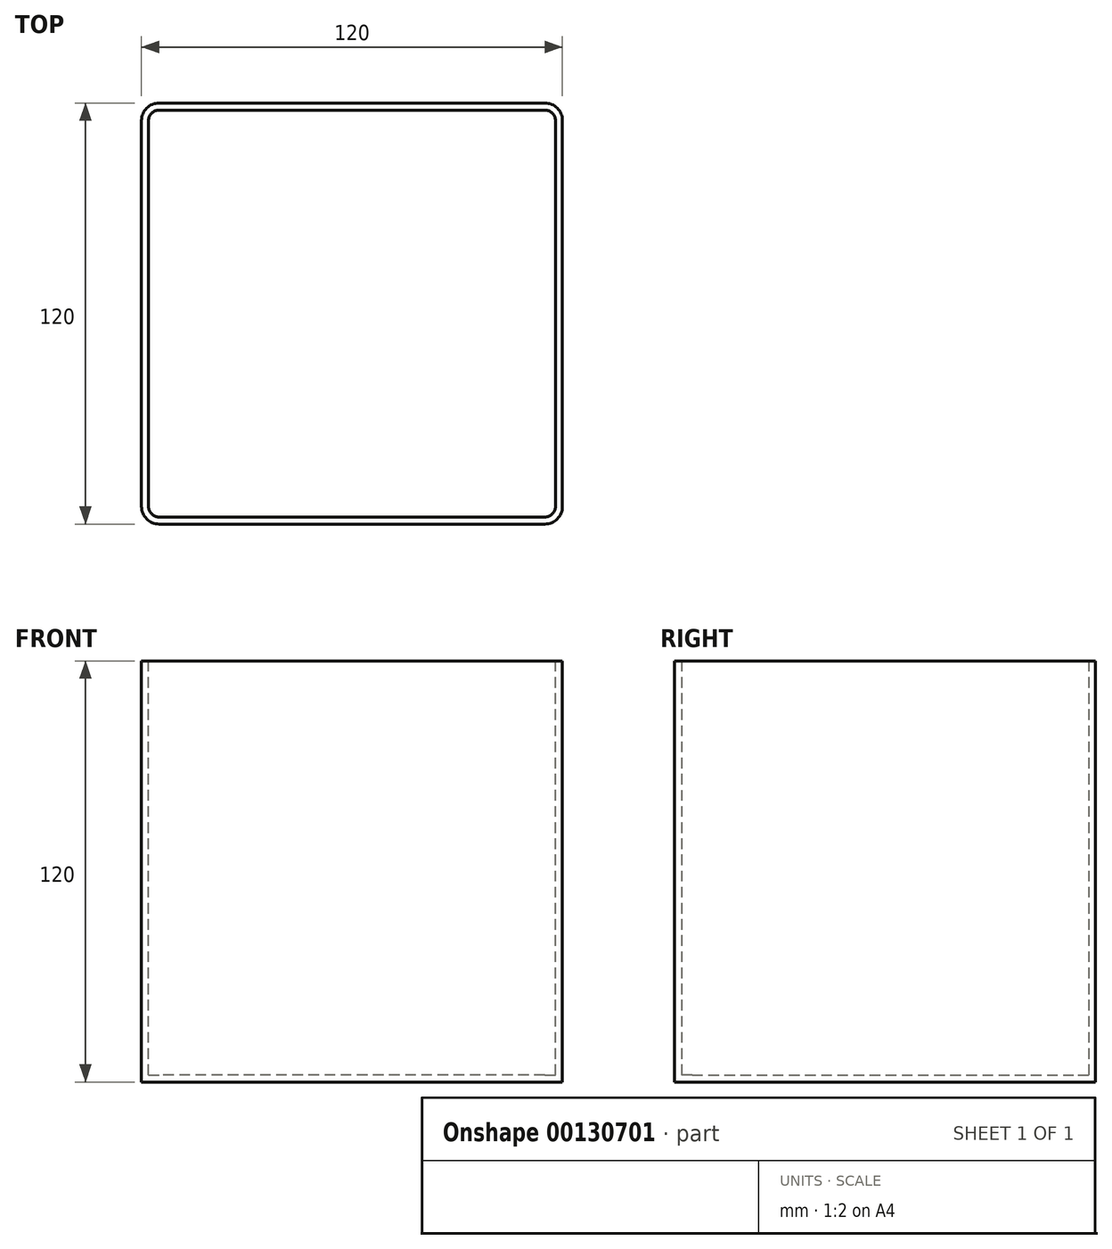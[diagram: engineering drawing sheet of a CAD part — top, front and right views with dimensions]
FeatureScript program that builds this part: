
annotation { "Feature Type Name" : "Feature", "Feature Type Description" : "" }
export const myFeature = defineFeature(function(context is Context, id is Id, definition is map)
    precondition{}
    {
        {
            var Q0;
            Q0=qCreatedBy(makeId("Top.planeOp"),FACE);
            var sketch = newSketch(context, id + "F0", { "sketchPlane" : qUnion([Q0])});
            skLineSegment(sketch, "E0.bottom", {"start": v(60, -60) * mm, "end": v(-60, -60) * mm});
            skLineSegment(sketch, "E0.top", {"start": v(60, 60) * mm, "end": v(-60, 60) * mm});
            skLineSegment(sketch, "E0.left", {"start": v(60, -60) * mm, "end": v(60, 60) * mm});
            skLineSegment(sketch, "E0.right", {"start": v(-60, -60) * mm, "end": v(-60, 60) * mm});
            skPoint(sketch, "E0.middle", {"position": v(0, 0) * mm});
            skSolve(sketch);
        }
        {
            var Q0;
            Q0=makeQuery(id+"F0.imprint","IMPRINT",FACE,{"disambiguationData":[TD([[makeQuery(id+"F0.imprint","IMPRINT",EDGE,{"derivedFrom":sQuery(id+"F0.wireOp",EDGE,"E0.bottom")}),-1.0]])]});
            extrude(context, id + "F1", {"entities" : qUnion([Q0]), "depth" : 120 * mm});
        }
        {
            var Q0;
            Q0=makeQuery(id+"F1.opExtrude","SWEPT_EDGE",EDGE,{"disambiguationData":[OSD([sQuery(id+"F0.wireOp",EDGE,"E0.bottom"),sQuery(id+"F0.wireOp",EDGE,"E0.right")])]});
            var Q1;
            Q1=makeQuery(id+"F1.opExtrude","SWEPT_EDGE",EDGE,{"disambiguationData":[OSD([sQuery(id+"F0.wireOp",EDGE,"E0.bottom"),sQuery(id+"F0.wireOp",EDGE,"E0.left")])]});
            var Q2;
            Q2=makeQuery(id+"F1.opExtrude","SWEPT_EDGE",EDGE,{"disambiguationData":[OSD([sQuery(id+"F0.wireOp",EDGE,"E0.top"),sQuery(id+"F0.wireOp",EDGE,"E0.left")])]});
            var Q3;
            Q3=makeQuery(id+"F1.opExtrude","SWEPT_EDGE",EDGE,{"disambiguationData":[OSD([sQuery(id+"F0.wireOp",EDGE,"E0.top"),sQuery(id+"F0.wireOp",EDGE,"E0.right")])]});
            fillet(context, id + "F2", {"entities" : qUnion([Q0, Q1, Q2, Q3]), "radius" : 5 * mm, "tangentPropagation" : true, "allowEdgeOverflow" : false});
        }
        {
            var Q0;
            Q0=makeQuery(id+"F1.opExtrude","CAP_FACE",FACE,{"disambiguationData":[OSD([sQuery(id+"F0.wireOp",EDGE,"E0.bottom"),sQuery(id+"F0.wireOp",EDGE,"E0.top"),sQuery(id+"F0.wireOp",EDGE,"E0.left"),sQuery(id+"F0.wireOp",EDGE,"E0.right")])],"isStart":false});
            shell(context, id + "F3", {"entities" : qUnion([Q0]), "thickness" : 2 * mm});
        }
    });
